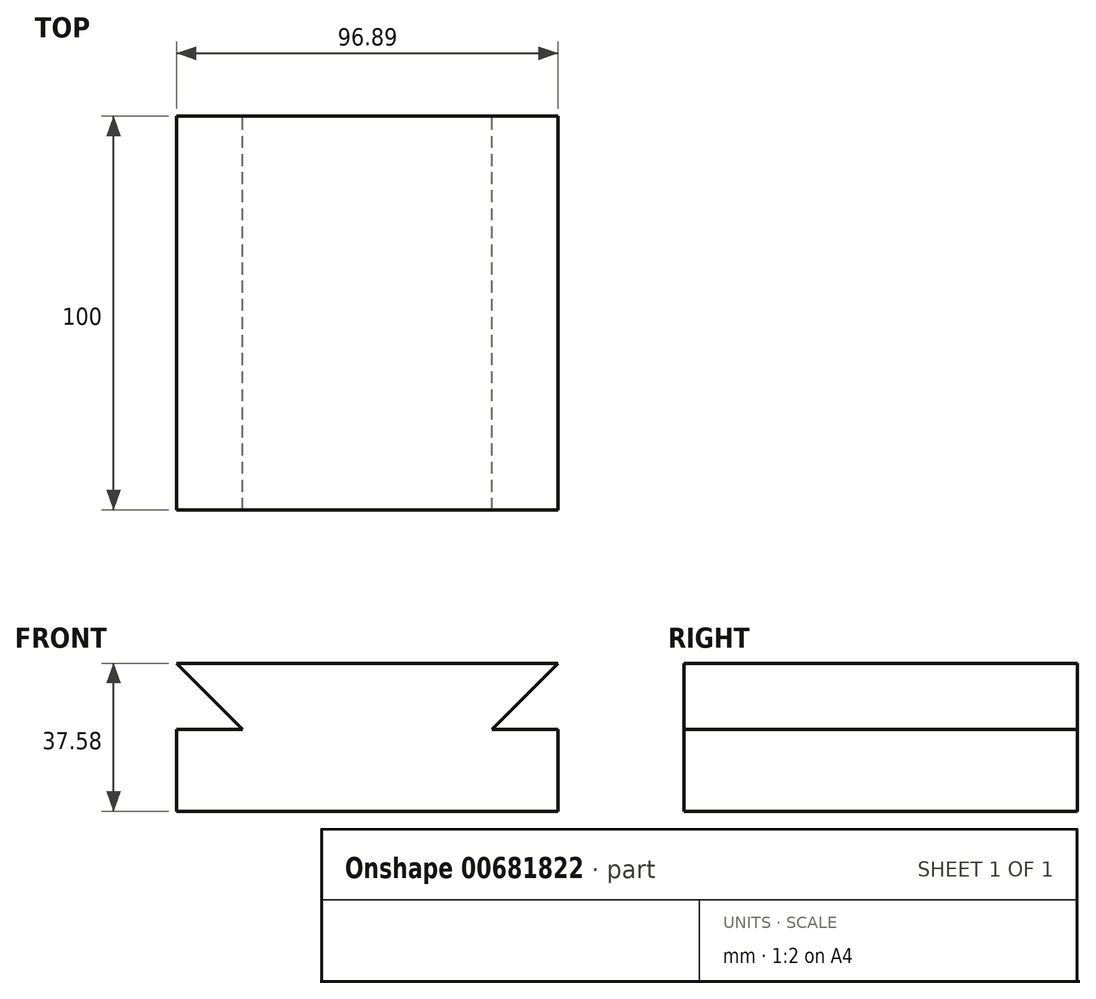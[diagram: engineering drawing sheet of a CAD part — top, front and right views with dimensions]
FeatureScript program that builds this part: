
annotation { "Feature Type Name" : "Feature", "Feature Type Description" : "" }
export const myFeature = defineFeature(function(context is Context, id is Id, definition is map)
    precondition{}
    {
        {
            var Q0;
            Q0=qCreatedBy(makeId("Front.planeOp"),FACE);
            var sketch = newSketch(context, id + "F0", { "sketchPlane" : qUnion([Q0])});
            skLineSegment(sketch, "E0", {"start": v(-16.88, 23.49) * mm, "end": v(31.56, 23.49) * mm});
            skLineSegment(sketch, "E1", {"start": v(31.56, 23.49) * mm, "end": v(14.83, 6.75) * mm});
            skLineSegment(sketch, "E2", {"start": v(14.83, 6.75) * mm, "end": v(31.56, 6.75) * mm});
            skLineSegment(sketch, "E3", {"start": v(31.56, 6.75) * mm, "end": v(31.56, -14.1) * mm});
            skLineSegment(sketch, "E4", {"start": v(31.56, -14.1) * mm, "end": v(-16.88, -14.1) * mm});
            skLineSegment(sketch, "E5", {"start": v(-16.88, 23.49) * mm, "end": v(-16.88, -14.1) * mm});
            skLineSegment(sketch, "E6.MirrorCS", {"start": v(-16.88, 23.49) * mm, "end": v(-65.33, 23.49) * mm});
            skLineSegment(sketch, "E7.MirrorCS", {"start": v(-65.33, 23.49) * mm, "end": v(-48.6, 6.75) * mm});
            skLineSegment(sketch, "E8.MirrorCS", {"start": v(-48.6, 6.75) * mm, "end": v(-65.33, 6.75) * mm});
            skLineSegment(sketch, "E9.MirrorCS", {"start": v(-65.33, 6.75) * mm, "end": v(-65.33, -14.1) * mm});
            skLineSegment(sketch, "E10.MirrorCS", {"start": v(-65.33, -14.1) * mm, "end": v(-16.88, -14.1) * mm});
            skSolve(sketch);
        }
        {
            var Q0;
            Q0 = qSketchRegion(id + "F0", true);
            extrude(context, id + "F1", {"entities" : qUnion([Q0]), "depth" : 100 * mm, "offsetDistance" : 25.4 * mm});
        }
    });
